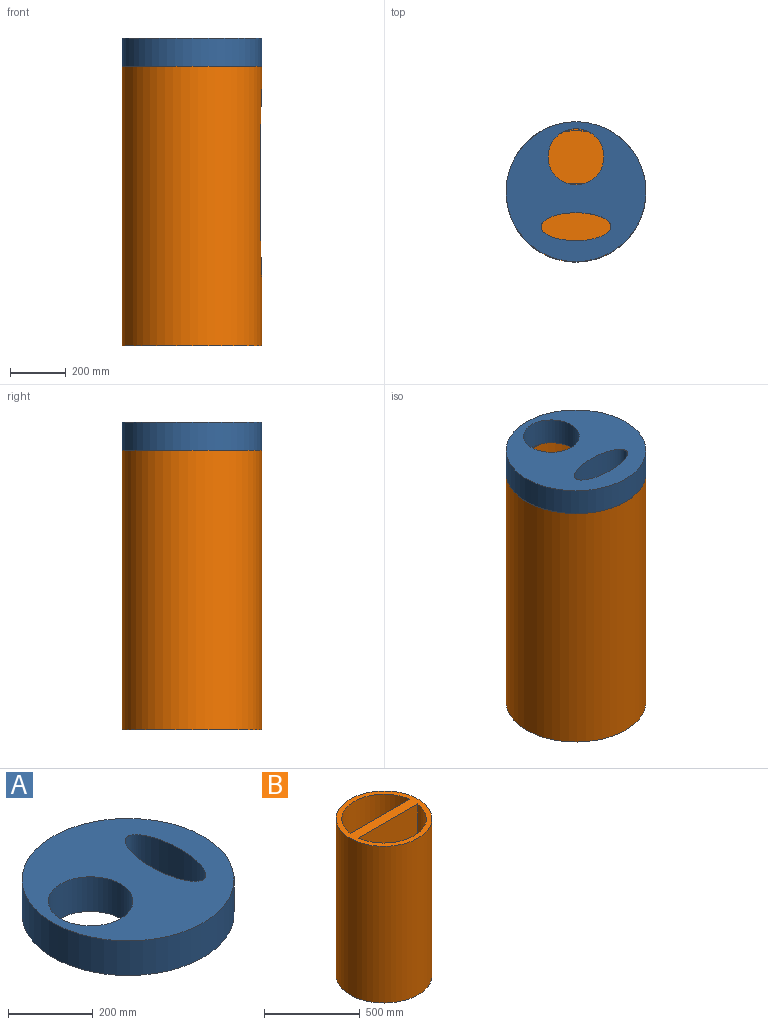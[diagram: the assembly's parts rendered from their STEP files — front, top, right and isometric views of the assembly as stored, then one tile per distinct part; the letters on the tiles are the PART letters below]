
ASSEMBLY  parts=2 mates=1
PART A: 5 faces, bbox 500x500x100 mm
  f0: cylinder r=250mm len=500mm, axis (0,0,-1), area 157079.6mm2, adj f1,f2
  f1: plane 500x500mm, normal (0,0,1), area 145298.7mm2, adj f0,f3,f4
  f2: plane 500x500mm, normal (0,0,-1), area 145298.7mm2, adj f0,f3,f4
  f3: extruded ~250x100mm, area 57540.4mm2, adj f1,f2
  f4: cylinder r=100mm len=200mm, axis (0,0,1), area 62831.9mm2, adj f1,f2
PART B: 11 faces, bbox 500x500x1000 mm
  f0: cylinder r=250mm len=1000mm, axis (0,0,-1), area 1501649mm2, adj f1,f2,f9
  f1: plane 500x500mm, normal (0,0,1), area 70614.4mm2, adj f0,f3,f4,f6,f7
  f2: plane 500x500mm, normal (0,0,-1), area 196349.5mm2, adj f0
  f3: cylinder r=220mm len=900mm, axis (0,0,1), area 567866.6mm2, adj f1,f4,f5
  f4: plane 900x435.89mm, normal (0,-1,0), area 392300.9mm2, adj f1,f3,f5
  f5: plane 435.89x190mm, normal (0,0,1), area 62867.6mm2, adj f3,f4
  f6: plane 900x435.89mm, normal (0,1,0), area 392300.9mm2, adj f1,f7,f8
  f7: cylinder r=220mm len=900mm, axis (0,0,1), area 567866.6mm2, adj f1,f6,f8
  f8: plane 435.89x190mm, normal (0,0,1), area 62867.6mm2, adj f6,f7
  f9: extruded ~747.29x117.02mm, area 31772.4mm2, adj f0,f10
  f10: plane 747.29x117.02mm, normal (1,0,0), area 68683.8mm2, adj f9
PLACE A rot(axis=(0,0,-1),90deg) t=(-459.76,-22.27,864.76)mm
PLACE B t=(-459.76,-22.27,-135.24)mm fixed
MATE cylindrical A.f0 <-> B.f7  axis (0,0,-1) through (-459.76,-22.27,864.76)mm
